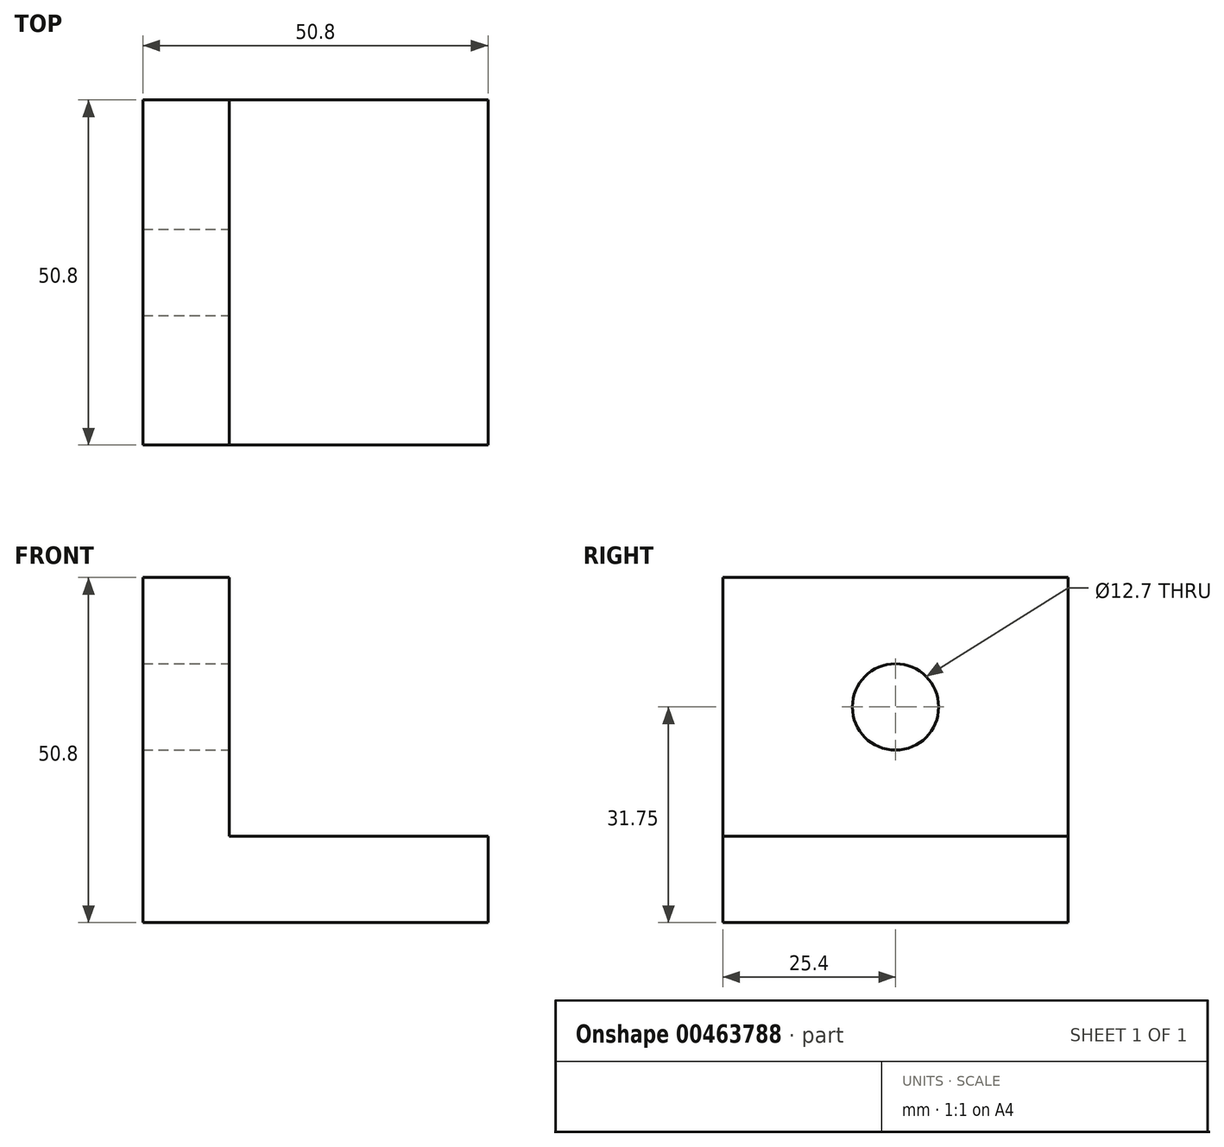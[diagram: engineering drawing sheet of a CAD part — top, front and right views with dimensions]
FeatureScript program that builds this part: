
annotation { "Feature Type Name" : "Feature", "Feature Type Description" : "" }
export const myFeature = defineFeature(function(context is Context, id is Id, definition is map)
    precondition{}
    {
        {
            var Q0;
            Q0=qCreatedBy(makeId("Front.planeOp"),FACE);
            var sketch = newSketch(context, id + "F0", { "sketchPlane" : qUnion([Q0])});
            skLineSegment(sketch, "E0", {"start": v(-65.76, 50.8) * mm, "end": v(-65.76, 0) * mm});
            skLineSegment(sketch, "E1", {"start": v(-65.76, 0) * mm, "end": v(-14.96, 0) * mm});
            skLineSegment(sketch, "E2", {"start": v(-14.96, 0) * mm, "end": v(-14.96, 12.7) * mm});
            skLineSegment(sketch, "E3", {"start": v(-14.96, 12.7) * mm, "end": v(-53.06, 12.7) * mm});
            skLineSegment(sketch, "E4", {"start": v(-53.06, 12.7) * mm, "end": v(-53.06, 50.8) * mm});
            skLineSegment(sketch, "E5", {"start": v(-53.06, 50.8) * mm, "end": v(-65.76, 50.8) * mm});
            skSolve(sketch);
        }
        {
            var Q0;
            Q0 = qSketchRegion(id + "F0", true);
            extrude(context, id + "F1", {"entities" : qUnion([Q0]), "depth" : 50.8 * mm});
        }
        {
            var Q0;
            Q0=makeQuery(id+"F1.opExtrude","SWEPT_FACE",FACE,{"disambiguationData":[OSD([sQuery(id+"F0.wireOp",EDGE,"E4")])]});
            var sketch = newSketch(context, id + "F2", { "sketchPlane" : qUnion([Q0])});
            skCircle(sketch, "E6", {"center": v(-25.4, 31.75) * mm, "radius": 6.35 * mm});
            skPoint(sketch, "E6.centerSnap0", {"position": v(0, 31.75) * mm});
            skPoint(sketch, "E6.centerSnap1", {"position": v(-25.4, 12.7) * mm});
            skSolve(sketch);
        }
        {
            var Q0;
            Q0=sQuery(id+"F2.wireOp",VERTEX,"E6.center");
            var Q1;
            Q1=makeQuery(id+"F1.opExtrude","SWEPT_BODY",BODY,{"disambiguationData":[OSD([sQuery(id+"F0.wireOp",EDGE,"E0"),sQuery(id+"F0.wireOp",EDGE,"E1"),sQuery(id+"F0.wireOp",EDGE,"E2"),sQuery(id+"F0.wireOp",EDGE,"E3"),sQuery(id+"F0.wireOp",EDGE,"E4"),sQuery(id+"F0.wireOp",EDGE,"E5")])]});
            hole(context, id + "F3", {"style" : HoleStyle.SIMPLE, "endStyle" : HoleEndStyle.THROUGH, "holeDiameter" : 12.7 * mm, "isTappedThrough" : true, "tappedDepth" : 12.7 * mm, "tapClearance" : 3, "locations" : qUnion([Q0]), "scope" : qUnion([Q1])});
        }
    });
